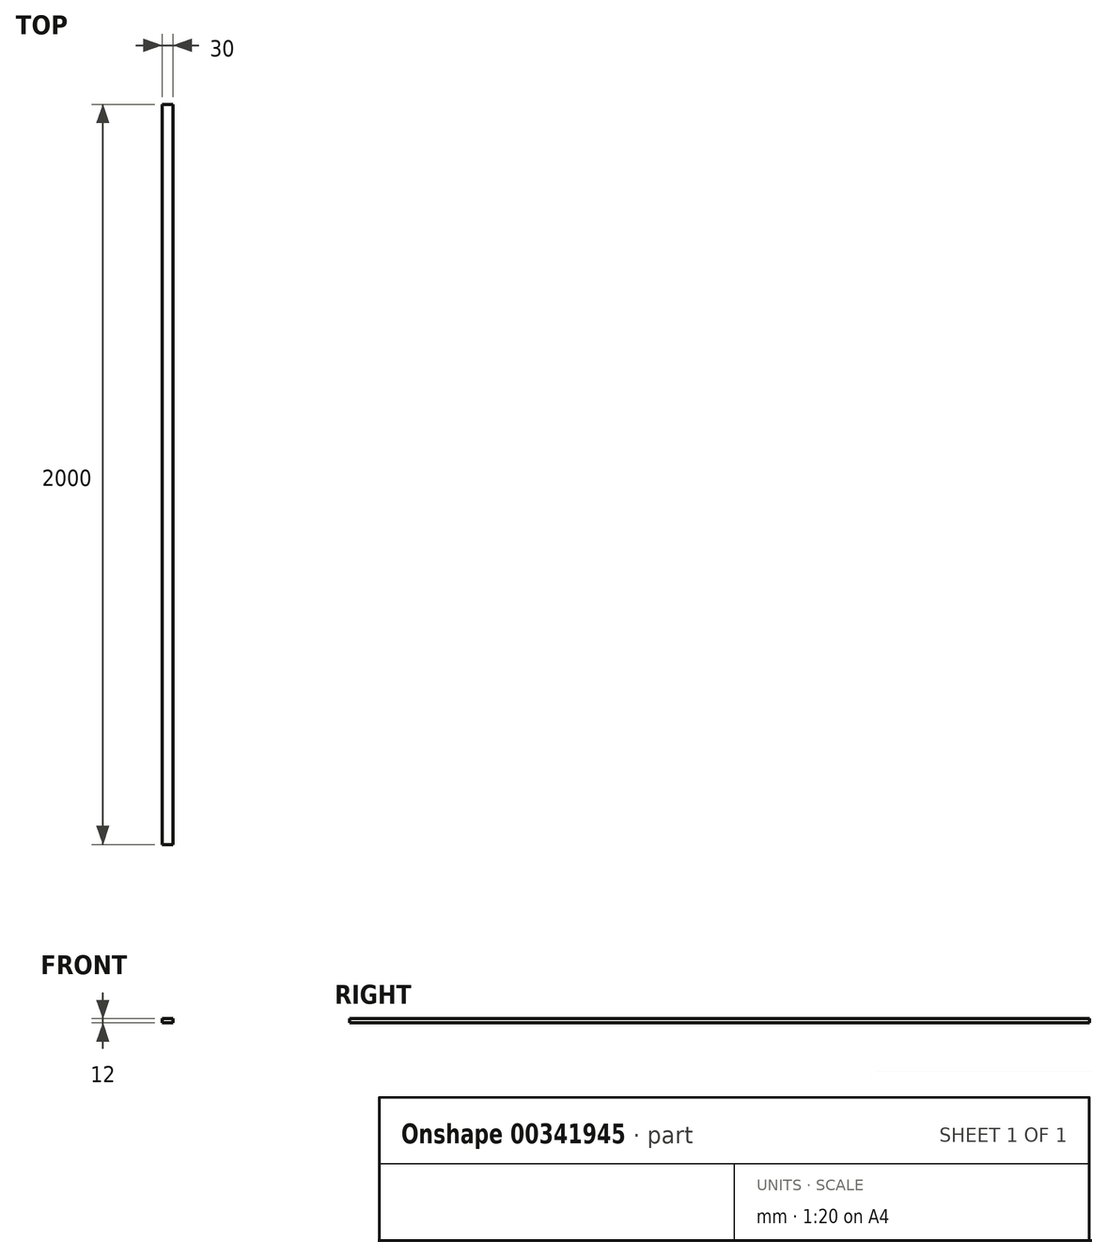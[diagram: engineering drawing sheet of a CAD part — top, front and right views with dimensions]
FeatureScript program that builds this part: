
annotation { "Feature Type Name" : "Feature", "Feature Type Description" : "" }
export const myFeature = defineFeature(function(context is Context, id is Id, definition is map)
    precondition{}
    {
        {
            var Q0;
            Q0=qCreatedBy(makeId("Front.planeOp"),FACE);
            var sketch = newSketch(context, id + "F0", { "sketchPlane" : qUnion([Q0])});
            skLineSegment(sketch, "E0.bottom", {"start": v(15, -6) * mm, "end": v(-15, -6) * mm});
            skLineSegment(sketch, "E0.top", {"start": v(15, 6) * mm, "end": v(-15, 6) * mm});
            skLineSegment(sketch, "E0.left", {"start": v(15, -6) * mm, "end": v(15, 6) * mm});
            skLineSegment(sketch, "E0.right", {"start": v(-15, -6) * mm, "end": v(-15, 6) * mm});
            skPoint(sketch, "E0.middle", {"position": v(0, 0) * mm});
            skSolve(sketch);
        }
        {
            var Q0;
            Q0 = qSketchRegion(id + "F0", true);
            extrude(context, id + "F1", {"entities" : qUnion([Q0]), "depth" : 1000 * mm, "hasSecondDirection" : true, "secondDirectionOppositeDirection" : true, "secondDirectionDepth" : 1000 * mm});
        }
    });
